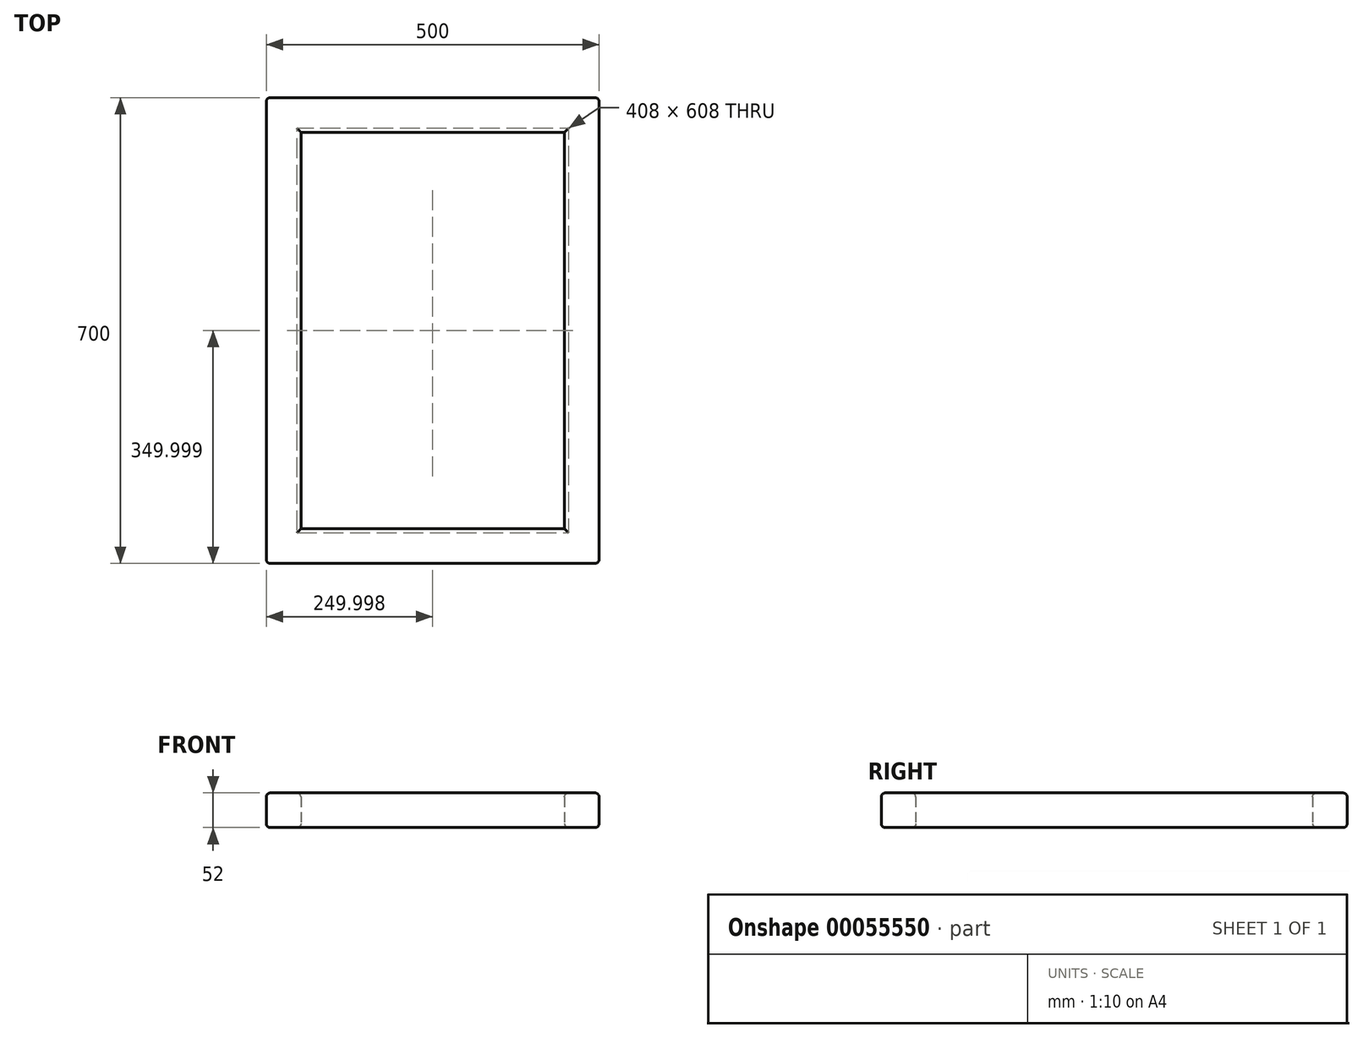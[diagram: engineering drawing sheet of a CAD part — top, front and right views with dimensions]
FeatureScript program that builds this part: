
annotation { "Feature Type Name" : "Feature", "Feature Type Description" : "" }
export const myFeature = defineFeature(function(context is Context, id is Id, definition is map)
    precondition{}
    {
        {
            var Q0;
            Q0=qCreatedBy(makeId("Top.planeOp"),FACE);
            var sketch = newSketch(context, id + "F0", { "sketchPlane" : qUnion([Q0])});
            skLineSegment(sketch, "E0.bottom", {"start": v(-279.35, 357) * mm, "end": v(220.65, 357) * mm});
            skLineSegment(sketch, "E0.top", {"start": v(-279.35, -343) * mm, "end": v(220.65, -343) * mm});
            skLineSegment(sketch, "E0.left", {"start": v(-279.35, 357) * mm, "end": v(-279.35, -343) * mm});
            skLineSegment(sketch, "E0.right", {"start": v(220.65, 357) * mm, "end": v(220.65, -343) * mm});
            skLineSegment(sketch, "E1.bottom", {"start": v(-227.35, 305) * mm, "end": v(168.65, 305) * mm});
            skLineSegment(sketch, "E1.top", {"start": v(-227.35, -291) * mm, "end": v(168.65, -291) * mm});
            skLineSegment(sketch, "E1.left", {"start": v(-227.35, 305) * mm, "end": v(-227.35, -291) * mm});
            skLineSegment(sketch, "E1.right", {"start": v(168.65, 305) * mm, "end": v(168.65, -291) * mm});
            skSolve(sketch);
        }
        {
            var Q0;
            Q0=makeQuery(id+"F0.imprint","IMPRINT",FACE,{"disambiguationData":[TD([[makeQuery(id+"F0.imprint","IMPRINT",EDGE,{"derivedFrom":sQuery(id+"F0.wireOp",EDGE,"E0.bottom")}),-1.0]])]});
            extrude(context, id + "F1", {"entities" : qUnion([Q0]), "depth" : 52 * mm});
        }
        {
            var Q0;
            Q0=makeQuery(id+"F1.opExtrude","CAP_FACE",FACE,{"disambiguationData":[OSD([sQuery(id+"F0.wireOp",EDGE,"E0.bottom"),sQuery(id+"F0.wireOp",EDGE,"E0.top"),sQuery(id+"F0.wireOp",EDGE,"E0.left"),sQuery(id+"F0.wireOp",EDGE,"E0.right"),sQuery(id+"F0.wireOp",EDGE,"E1.bottom"),sQuery(id+"F0.wireOp",EDGE,"E1.top"),sQuery(id+"F0.wireOp",EDGE,"E1.left"),sQuery(id+"F0.wireOp",EDGE,"E1.right")])],"isStart":true});
            var Q1;
            Q1=makeQuery(id+"F1.opExtrude","CAP_FACE",FACE,{"disambiguationData":[OSD([sQuery(id+"F0.wireOp",EDGE,"E0.bottom"),sQuery(id+"F0.wireOp",EDGE,"E0.top"),sQuery(id+"F0.wireOp",EDGE,"E0.left"),sQuery(id+"F0.wireOp",EDGE,"E0.right"),sQuery(id+"F0.wireOp",EDGE,"E1.bottom"),sQuery(id+"F0.wireOp",EDGE,"E1.top"),sQuery(id+"F0.wireOp",EDGE,"E1.left"),sQuery(id+"F0.wireOp",EDGE,"E1.right")])],"isStart":false});
            var Q2;
            Q2=makeQuery(id+"F1.opExtrude","SWEPT_EDGE",EDGE,{"disambiguationData":[OSD([sQuery(id+"F0.wireOp",EDGE,"E0.bottom"),sQuery(id+"F0.wireOp",EDGE,"E0.left")])]});
            var Q3;
            Q3=makeQuery(id+"F1.opExtrude","SWEPT_EDGE",EDGE,{"disambiguationData":[OSD([sQuery(id+"F0.wireOp",EDGE,"E0.top"),sQuery(id+"F0.wireOp",EDGE,"E0.left")])]});
            var Q4;
            Q4=makeQuery(id+"F1.opExtrude","SWEPT_EDGE",EDGE,{"disambiguationData":[OSD([sQuery(id+"F0.wireOp",EDGE,"E0.top"),sQuery(id+"F0.wireOp",EDGE,"E0.right")])]});
            var Q5;
            Q5=makeQuery(id+"F1.opExtrude","SWEPT_EDGE",EDGE,{"disambiguationData":[OSD([sQuery(id+"F0.wireOp",EDGE,"E0.bottom"),sQuery(id+"F0.wireOp",EDGE,"E0.right")])]});
            fillet(context, id + "F2", {"entities" : qUnion([Q0, Q1, Q2, Q3, Q4, Q5]), "radius" : 6 * mm, "tangentPropagation" : true, "allowEdgeOverflow" : false});
        }
    });
